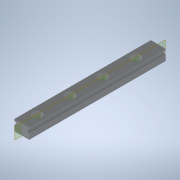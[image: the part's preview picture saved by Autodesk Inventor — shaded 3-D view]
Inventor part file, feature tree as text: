
AUTODESK INVENTOR PART (.ipt)
format: ipt  version: 2022 (Build 260153000, 153)  size: 129,024 bytes
history: imported  units: mm
features: plane x1, other x1, imported_body x1
ambient origin geometry x8: Origin, YZ Plane, XZ Plane, XY Plane, X Axis, Y Axis, Z Axis, Center Point
bodies: Volumenkörper1 (imported_parasolid)
feature tree (3):
  plane  "Arbeitsebene1"
  other  "LPattern1"
  imported_body  NMx_Import_Brep_tag  [imported B-rep: ~30 faces, bbox_mm=[9.0, 6.5, 83.0]]
